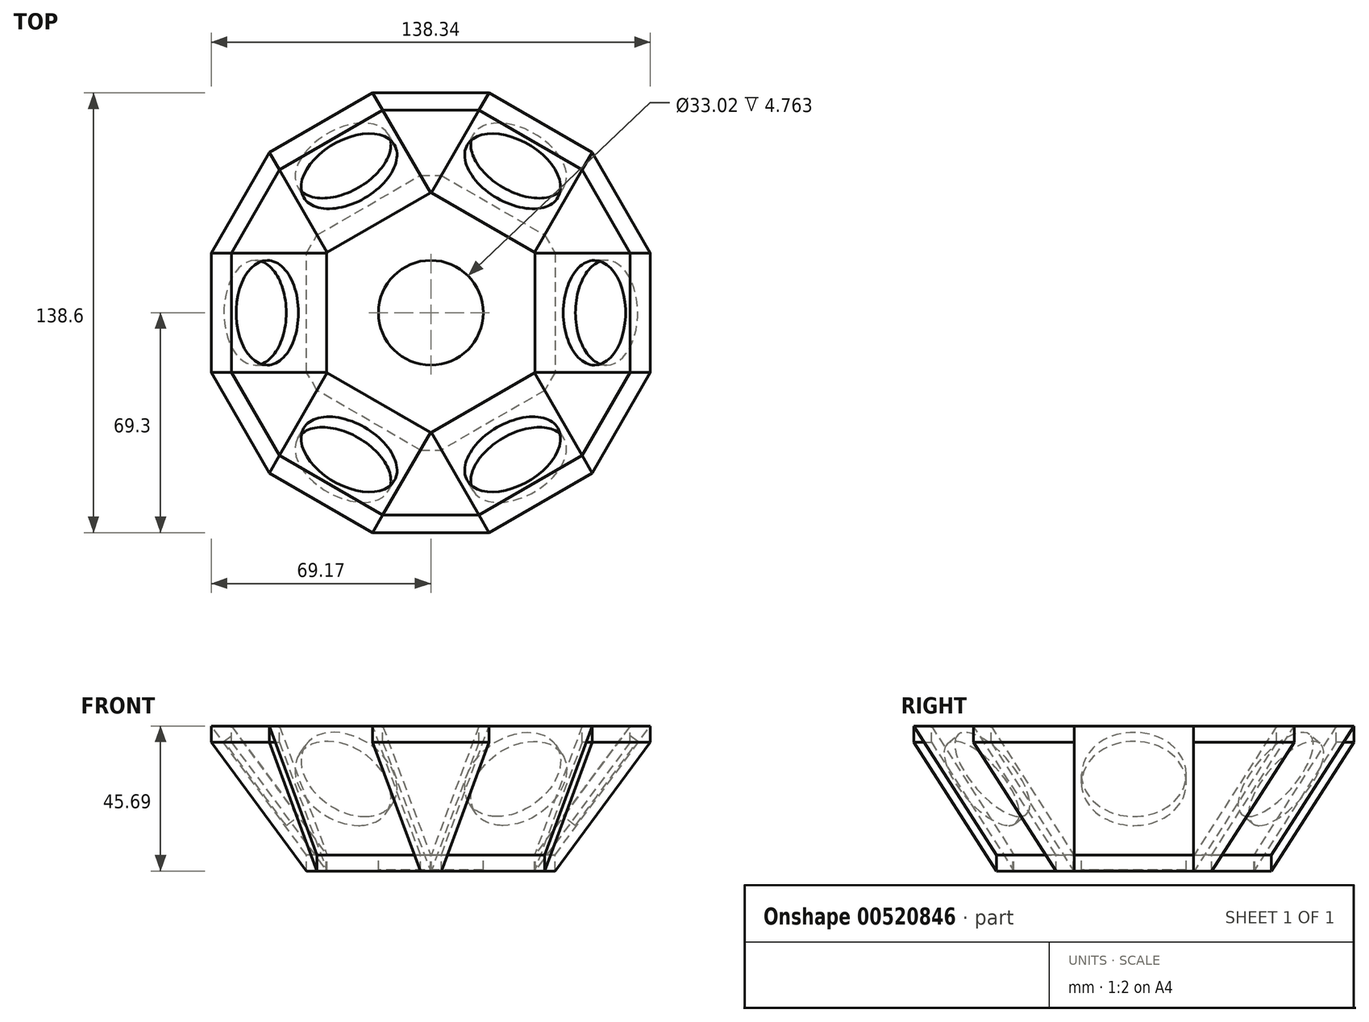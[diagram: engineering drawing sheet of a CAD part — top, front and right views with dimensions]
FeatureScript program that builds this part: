
annotation { "Feature Type Name" : "Feature", "Feature Type Description" : "" }
export const myFeature = defineFeature(function(context is Context, id is Id, definition is map)
    precondition{}
    {
        {
            var Q0;
            Q0=qCreatedBy(makeId("Top.planeOp"),FACE);
            var sketch = newSketch(context, id + "F0", { "sketchPlane" : qUnion([Q0])});
            skCircle(sketch, "E0.cCircle", {"center": v(0, 0) * mm, "radius": 33 * mm, "construction": true});
            skLineSegment(sketch, "E0.0", {"start": v(33, 19.05) * mm, "end": v(33, -19.05) * mm});
            skLineSegment(sketch, "E0.1", {"start": v(33, -19.05) * mm, "end": v(0, -38.1) * mm});
            skLineSegment(sketch, "E0.2", {"start": v(0, -38.1) * mm, "end": v(-33, -19.05) * mm});
            skLineSegment(sketch, "E0.3", {"start": v(-33, -19.05) * mm, "end": v(-33, 19.05) * mm});
            skLineSegment(sketch, "E0.4", {"start": v(-33, 19.05) * mm, "end": v(0, 38.1) * mm});
            skLineSegment(sketch, "E0.5", {"start": v(0, 38.1) * mm, "end": v(33, 19.05) * mm});
            skPoint(sketch, "E0.0.midPoint", {"position": v(33, 0) * mm});
            skSolve(sketch);
        }
        {
            var Q0;
            Q0=qCreatedBy(makeId("Front.planeOp"),FACE);
            var sketch = newSketch(context, id + "F1", { "sketchPlane" : qUnion([Q0])});
            skLineSegment(sketch, "E1", {"start": v(-32.8, 0) * mm, "end": v(-39.14, 0) * mm});
            skLineSegment(sketch, "E2", {"start": v(-39.14, 0) * mm, "end": v(-69.17, 40.61) * mm});
            skLineSegment(sketch, "E3", {"start": v(-69.17, 40.61) * mm, "end": v(-62.82, 40.61) * mm});
            skLineSegment(sketch, "E4", {"start": v(-62.82, 40.61) * mm, "end": v(-32.8, 0) * mm});
            skSolve(sketch);
        }
        {
            var Q0;
            Q0 = qSketchRegion(id + "F1", true);
            extrude(context, id + "F2", {"entities" : qUnion([Q0]), "depth" : 19.05 * mm, "offsetDistance" : 25.4 * mm});
        }
        {
            var Q0;
            Q0=makeQuery(id+"F2.opExtrude","CAP_FACE",FACE,{"disambiguationData":[OSD([sQuery(id+"F1.wireOp",EDGE,"E1"),sQuery(id+"F1.wireOp",EDGE,"E2"),sQuery(id+"F1.wireOp",EDGE,"E3"),sQuery(id+"F1.wireOp",EDGE,"E4")])],"isStart":true});
            extrude(context, id + "F3", {"entities" : qUnion([Q0]), "operationType" : NewBodyOperationType.ADD, "depth" : 19.05 * mm, "offsetDistance" : 25.4 * mm});
        }
        {
            var Q0;
            {var subQ0=sQuery(id+"F1.wireOp",EDGE,"E4");Q0=makeQuery(id+"F3.boolean.opBoolean","MERGE",FACE,{"derivedFrom":[makeQuery(id+"F2.opExtrude","SWEPT_FACE",FACE,{"disambiguationData":[OSD([subQ0])]}),makeQuery(id+"F3.opExtrude","SWEPT_FACE",FACE,{"disambiguationData":[OSD([subQ0])]})]});}
            var sketch = newSketch(context, id + "F4", { "sketchPlane" : qUnion([Q0])});
            skCircle(sketch, "E5", {"center": v(0, 51.05) * mm, "radius": 16.51 * mm});
            skSolve(sketch);
        }
        {
            var Q0;
            Q0=makeQuery(id+"F4.imprint","IMPRINT",FACE,{"disambiguationData":[TD([[makeQuery(id+"F4.imprint","IMPRINT",EDGE,{"derivedFrom":sQuery(id+"F4.wireOp",EDGE,"E5")}),1.0]])]});
            extrude(context, id + "F5", {"entities" : qUnion([Q0]), "operationType" : NewBodyOperationType.REMOVE, "oppositeDirection" : true, "depth" : 4.76 * mm, "offsetDistance" : 25.4 * mm});
        }
        {
            var Q0;
            Q0=makeQuery(id+"F2.opExtrude","CAP_FACE",FACE,{"disambiguationData":[OSD([sQuery(id+"F1.wireOp",EDGE,"E1"),sQuery(id+"F1.wireOp",EDGE,"E2"),sQuery(id+"F1.wireOp",EDGE,"E3"),sQuery(id+"F1.wireOp",EDGE,"E4")])],"isStart":false});
            extrude(context, id + "F6", {"entities" : qUnion([Q0]), "operationType" : NewBodyOperationType.REMOVE, "oppositeDirection" : true, "depth" : 0.25 * mm, "offsetDistance" : 25.4 * mm});
        }
        {
            var Q0;
            Q0=makeQuery(id+"F3.opExtrude","CAP_FACE",FACE,{"disambiguationData":[OSD([sQuery(id+"F1.wireOp",EDGE,"E1"),sQuery(id+"F1.wireOp",EDGE,"E2"),sQuery(id+"F1.wireOp",EDGE,"E3"),sQuery(id+"F1.wireOp",EDGE,"E4")])],"isStart":false});
            extrude(context, id + "F7", {"entities" : qUnion([Q0]), "operationType" : NewBodyOperationType.REMOVE, "oppositeDirection" : true, "depth" : 0.25 * mm, "offsetDistance" : 25.4 * mm});
        }
        {
            var Q0;
            Q0=makeQuery(id+"F2.opExtrude","SWEPT_BODY",BODY,{"disambiguationData":[OSD([sQuery(id+"F1.wireOp",EDGE,"E1"),sQuery(id+"F1.wireOp",EDGE,"E2"),sQuery(id+"F1.wireOp",EDGE,"E3"),sQuery(id+"F1.wireOp",EDGE,"E4")])]});
            var Q1;
            Q1=sQuery(id+"F0.wireOp",EDGE,"E0.cCircle");
            circularPattern(context, id + "F8", {"entities" : qUnion([Q0]), "axis" : qUnion([Q1]), "angle" : 360 * degree, "instanceCount" : 6, "equalSpace" : true, "isCentered" : true});
        }
        {
            var Q0;
            Q0=makeQuery(id+"F8.opPattern","COPY",FACE,{"derivedFrom":makeQuery(id+"F6.boolean.opBoolean","COPY",FACE,{"derivedFrom":makeQuery(id+"F6.opExtrude","CAP_FACE",FACE,{"disambiguationData":[OSD([sQuery(id+"F1.wireOp",EDGE,"E1"),sQuery(id+"F1.wireOp",EDGE,"E2"),sQuery(id+"F1.wireOp",EDGE,"E3"),sQuery(id+"F1.wireOp",EDGE,"E4")])],"isStart":false})}),"instanceName":"1"});
            var Q1;
            Q1=makeQuery(id+"F8.opPattern","COPY",FACE,{"derivedFrom":makeQuery(id+"F7.boolean.opBoolean","COPY",FACE,{"derivedFrom":makeQuery(id+"F7.opExtrude","CAP_FACE",FACE,{"disambiguationData":[OSD([sQuery(id+"F1.wireOp",EDGE,"E1"),sQuery(id+"F1.wireOp",EDGE,"E2"),sQuery(id+"F1.wireOp",EDGE,"E3"),sQuery(id+"F1.wireOp",EDGE,"E4")])],"isStart":false})}),"instanceName":"-4"});
            loft(context, id + "F9", {"sheetProfilesArray" : [{ "sheetProfileEntities" : qUnion([Q0]) }, { "sheetProfileEntities" : qUnion([Q1]) }]});
        }
        {
            var Q0;
            Q0=makeQuery(id+"F8.opPattern","COPY",FACE,{"derivedFrom":makeQuery(id+"F7.boolean.opBoolean","COPY",FACE,{"derivedFrom":makeQuery(id+"F7.opExtrude","CAP_FACE",FACE,{"disambiguationData":[OSD([sQuery(id+"F1.wireOp",EDGE,"E1"),sQuery(id+"F1.wireOp",EDGE,"E2"),sQuery(id+"F1.wireOp",EDGE,"E3"),sQuery(id+"F1.wireOp",EDGE,"E4")])],"isStart":false})}),"instanceName":"1"});
            var Q1;
            Q1=makeQuery(id+"F6.boolean.opBoolean","COPY",FACE,{"derivedFrom":makeQuery(id+"F6.opExtrude","CAP_FACE",FACE,{"disambiguationData":[OSD([sQuery(id+"F1.wireOp",EDGE,"E1"),sQuery(id+"F1.wireOp",EDGE,"E2"),sQuery(id+"F1.wireOp",EDGE,"E3"),sQuery(id+"F1.wireOp",EDGE,"E4")])],"isStart":false})});
            loft(context, id + "F10", {"sheetProfilesArray" : [{ "sheetProfileEntities" : qUnion([Q0]) }, { "sheetProfileEntities" : qUnion([Q1]) }]});
        }
        {
            var Q0;
            Q0=makeQuery(id+"F7.boolean.opBoolean","COPY",FACE,{"derivedFrom":makeQuery(id+"F7.opExtrude","CAP_FACE",FACE,{"disambiguationData":[OSD([sQuery(id+"F1.wireOp",EDGE,"E1"),sQuery(id+"F1.wireOp",EDGE,"E2"),sQuery(id+"F1.wireOp",EDGE,"E3"),sQuery(id+"F1.wireOp",EDGE,"E4")])],"isStart":false})});
            var Q1;
            Q1=makeQuery(id+"F8.opPattern","COPY",FACE,{"derivedFrom":makeQuery(id+"F6.boolean.opBoolean","COPY",FACE,{"derivedFrom":makeQuery(id+"F6.opExtrude","CAP_FACE",FACE,{"disambiguationData":[OSD([sQuery(id+"F1.wireOp",EDGE,"E1"),sQuery(id+"F1.wireOp",EDGE,"E2"),sQuery(id+"F1.wireOp",EDGE,"E3"),sQuery(id+"F1.wireOp",EDGE,"E4")])],"isStart":false})}),"instanceName":"-1"});
            loft(context, id + "F11", {"sheetProfilesArray" : [{ "sheetProfileEntities" : qUnion([Q0]) }, { "sheetProfileEntities" : qUnion([Q1]) }]});
        }
        {
            var Q0;
            Q0=makeQuery(id+"F8.opPattern","COPY",FACE,{"derivedFrom":makeQuery(id+"F7.boolean.opBoolean","COPY",FACE,{"derivedFrom":makeQuery(id+"F7.opExtrude","CAP_FACE",FACE,{"disambiguationData":[OSD([sQuery(id+"F1.wireOp",EDGE,"E1"),sQuery(id+"F1.wireOp",EDGE,"E2"),sQuery(id+"F1.wireOp",EDGE,"E3"),sQuery(id+"F1.wireOp",EDGE,"E4")])],"isStart":false})}),"instanceName":"-1"});
            var Q1;
            Q1=makeQuery(id+"F8.opPattern","COPY",FACE,{"derivedFrom":makeQuery(id+"F6.boolean.opBoolean","COPY",FACE,{"derivedFrom":makeQuery(id+"F6.opExtrude","CAP_FACE",FACE,{"disambiguationData":[OSD([sQuery(id+"F1.wireOp",EDGE,"E1"),sQuery(id+"F1.wireOp",EDGE,"E2"),sQuery(id+"F1.wireOp",EDGE,"E3"),sQuery(id+"F1.wireOp",EDGE,"E4")])],"isStart":false})}),"instanceName":"-2"});
            loft(context, id + "F12", {"sheetProfilesArray" : [{ "sheetProfileEntities" : qUnion([Q0]) }, { "sheetProfileEntities" : qUnion([Q1]) }]});
        }
        {
            var Q0;
            Q0=makeQuery(id+"F8.opPattern","COPY",FACE,{"derivedFrom":makeQuery(id+"F7.boolean.opBoolean","COPY",FACE,{"derivedFrom":makeQuery(id+"F7.opExtrude","CAP_FACE",FACE,{"disambiguationData":[OSD([sQuery(id+"F1.wireOp",EDGE,"E1"),sQuery(id+"F1.wireOp",EDGE,"E2"),sQuery(id+"F1.wireOp",EDGE,"E3"),sQuery(id+"F1.wireOp",EDGE,"E4")])],"isStart":false})}),"instanceName":"-2"});
            var Q1;
            Q1=makeQuery(id+"F8.opPattern","COPY",FACE,{"derivedFrom":makeQuery(id+"F6.boolean.opBoolean","COPY",FACE,{"derivedFrom":makeQuery(id+"F6.opExtrude","CAP_FACE",FACE,{"disambiguationData":[OSD([sQuery(id+"F1.wireOp",EDGE,"E1"),sQuery(id+"F1.wireOp",EDGE,"E2"),sQuery(id+"F1.wireOp",EDGE,"E3"),sQuery(id+"F1.wireOp",EDGE,"E4")])],"isStart":false})}),"instanceName":"-3"});
            loft(context, id + "F13", {"sheetProfilesArray" : [{ "sheetProfileEntities" : qUnion([Q0]) }, { "sheetProfileEntities" : qUnion([Q1]) }]});
        }
        {
            var Q0;
            Q0=makeQuery(id+"F8.opPattern","COPY",FACE,{"derivedFrom":makeQuery(id+"F7.boolean.opBoolean","COPY",FACE,{"derivedFrom":makeQuery(id+"F7.opExtrude","CAP_FACE",FACE,{"disambiguationData":[OSD([sQuery(id+"F1.wireOp",EDGE,"E1"),sQuery(id+"F1.wireOp",EDGE,"E2"),sQuery(id+"F1.wireOp",EDGE,"E3"),sQuery(id+"F1.wireOp",EDGE,"E4")])],"isStart":false})}),"instanceName":"-3"});
            var Q1;
            Q1=makeQuery(id+"F8.opPattern","COPY",FACE,{"derivedFrom":makeQuery(id+"F6.boolean.opBoolean","COPY",FACE,{"derivedFrom":makeQuery(id+"F6.opExtrude","CAP_FACE",FACE,{"disambiguationData":[OSD([sQuery(id+"F1.wireOp",EDGE,"E1"),sQuery(id+"F1.wireOp",EDGE,"E2"),sQuery(id+"F1.wireOp",EDGE,"E3"),sQuery(id+"F1.wireOp",EDGE,"E4")])],"isStart":false})}),"instanceName":"-4"});
            loft(context, id + "F14", {"sheetProfilesArray" : [{ "sheetProfileEntities" : qUnion([Q0]) }, { "sheetProfileEntities" : qUnion([Q1]) }]});
        }
        {
            var Q0;
            Q0 = qSketchRegion(id + "F0", true);
            extrude(context, id + "F15", {"entities" : qUnion([Q0]), "oppositeDirection" : true, "depth" : 5.08 * mm, "offsetDistance" : 25.4 * mm});
        }
        {
            var Q0;
            {var subQ0=sQuery(id+"F1.wireOp",EDGE,"E1");Q0=makeQuery(id+"F8.opPattern","COPY",FACE,{"derivedFrom":makeQuery(id+"F3.boolean.opBoolean","MERGE",FACE,{"derivedFrom":[makeQuery(id+"F2.opExtrude","SWEPT_FACE",FACE,{"disambiguationData":[OSD([subQ0])]}),makeQuery(id+"F3.opExtrude","SWEPT_FACE",FACE,{"disambiguationData":[OSD([subQ0])]})]}),"instanceName":"-1"});}
            var Q1;
            Q1=makeQuery(id+"F11.opLoft","SWEPT_FACE",FACE,{"disambiguationData":[OSD([sQuery(id+"F1.wireOp",EDGE,"E1"),sQuery(id+"F1.wireOp",EDGE,"E2"),sQuery(id+"F1.wireOp",EDGE,"E4")])]});
            var Q2;
            {var subQ0=sQuery(id+"F1.wireOp",EDGE,"E1");Q2=makeQuery(id+"F3.boolean.opBoolean","MERGE",FACE,{"derivedFrom":[makeQuery(id+"F2.opExtrude","SWEPT_FACE",FACE,{"disambiguationData":[OSD([subQ0])]}),makeQuery(id+"F3.opExtrude","SWEPT_FACE",FACE,{"disambiguationData":[OSD([subQ0])]})]});}
            var Q3;
            {var subQ0=sQuery(id+"F1.wireOp",EDGE,"E1");Q3=makeQuery(id+"F8.opPattern","COPY",FACE,{"derivedFrom":makeQuery(id+"F3.boolean.opBoolean","MERGE",FACE,{"derivedFrom":[makeQuery(id+"F2.opExtrude","SWEPT_FACE",FACE,{"disambiguationData":[OSD([subQ0])]}),makeQuery(id+"F3.opExtrude","SWEPT_FACE",FACE,{"disambiguationData":[OSD([subQ0])]})]}),"instanceName":"1"});}
            var Q4;
            Q4=makeQuery(id+"F10.opLoft","SWEPT_FACE",FACE,{"disambiguationData":[OSD([sQuery(id+"F1.wireOp",EDGE,"E1"),sQuery(id+"F1.wireOp",EDGE,"E2"),sQuery(id+"F1.wireOp",EDGE,"E4")])]});
            var Q5;
            Q5=makeQuery(id+"F9.opLoft","SWEPT_FACE",FACE,{"disambiguationData":[OSD([sQuery(id+"F1.wireOp",EDGE,"E1"),sQuery(id+"F1.wireOp",EDGE,"E2"),sQuery(id+"F1.wireOp",EDGE,"E4")])]});
            var Q6;
            {var subQ0=sQuery(id+"F1.wireOp",EDGE,"E1");Q6=makeQuery(id+"F8.opPattern","COPY",FACE,{"derivedFrom":makeQuery(id+"F3.boolean.opBoolean","MERGE",FACE,{"derivedFrom":[makeQuery(id+"F2.opExtrude","SWEPT_FACE",FACE,{"disambiguationData":[OSD([subQ0])]}),makeQuery(id+"F3.opExtrude","SWEPT_FACE",FACE,{"disambiguationData":[OSD([subQ0])]})]}),"instanceName":"-4"});}
            var Q7;
            Q7=makeQuery(id+"F14.opLoft","SWEPT_FACE",FACE,{"disambiguationData":[OSD([sQuery(id+"F1.wireOp",EDGE,"E1"),sQuery(id+"F1.wireOp",EDGE,"E2"),sQuery(id+"F1.wireOp",EDGE,"E4")])]});
            var Q8;
            {var subQ0=sQuery(id+"F1.wireOp",EDGE,"E1");Q8=makeQuery(id+"F8.opPattern","COPY",FACE,{"derivedFrom":makeQuery(id+"F3.boolean.opBoolean","MERGE",FACE,{"derivedFrom":[makeQuery(id+"F2.opExtrude","SWEPT_FACE",FACE,{"disambiguationData":[OSD([subQ0])]}),makeQuery(id+"F3.opExtrude","SWEPT_FACE",FACE,{"disambiguationData":[OSD([subQ0])]})]}),"instanceName":"-3"});}
            var Q9;
            Q9=makeQuery(id+"F13.opLoft","SWEPT_FACE",FACE,{"disambiguationData":[OSD([sQuery(id+"F1.wireOp",EDGE,"E1"),sQuery(id+"F1.wireOp",EDGE,"E2"),sQuery(id+"F1.wireOp",EDGE,"E4")])]});
            var Q10;
            {var subQ0=sQuery(id+"F1.wireOp",EDGE,"E1");Q10=makeQuery(id+"F8.opPattern","COPY",FACE,{"derivedFrom":makeQuery(id+"F3.boolean.opBoolean","MERGE",FACE,{"derivedFrom":[makeQuery(id+"F2.opExtrude","SWEPT_FACE",FACE,{"disambiguationData":[OSD([subQ0])]}),makeQuery(id+"F3.opExtrude","SWEPT_FACE",FACE,{"disambiguationData":[OSD([subQ0])]})]}),"instanceName":"-2"});}
            var Q11;
            Q11=makeQuery(id+"F12.opLoft","SWEPT_FACE",FACE,{"disambiguationData":[OSD([sQuery(id+"F1.wireOp",EDGE,"E1"),sQuery(id+"F1.wireOp",EDGE,"E2"),sQuery(id+"F1.wireOp",EDGE,"E4")])]});
            extrude(context, id + "F16", {"entities" : qUnion([Q0, Q1, Q2, Q3, Q4, Q5, Q6, Q7, Q8, Q9, Q10, Q11]), "depth" : 5.08 * mm, "offsetDistance" : 25.4 * mm});
        }
        {
            var Q0;
            Q0=makeQuery(id+"F15.opExtrude","CAP_FACE",FACE,{"disambiguationData":[OSD([sQuery(id+"F0.wireOp",EDGE,"E0.0"),sQuery(id+"F0.wireOp",EDGE,"E0.1"),sQuery(id+"F0.wireOp",EDGE,"E0.2"),sQuery(id+"F0.wireOp",EDGE,"E0.3"),sQuery(id+"F0.wireOp",EDGE,"E0.4"),sQuery(id+"F0.wireOp",EDGE,"E0.5")])],"isStart":true});
            var sketch = newSketch(context, id + "F17", { "sketchPlane" : qUnion([Q0])});
            skCircle(sketch, "E6", {"center": v(0, 0) * mm, "radius": 16.51 * mm});
            skSolve(sketch);
        }
        {
            var Q0;
            Q0 = qSketchRegion(id + "F17", true);
            extrude(context, id + "F18", {"entities" : qUnion([Q0]), "operationType" : NewBodyOperationType.REMOVE, "oppositeDirection" : true, "depth" : 4.76 * mm, "offsetDistance" : 25.4 * mm});
        }
    });
